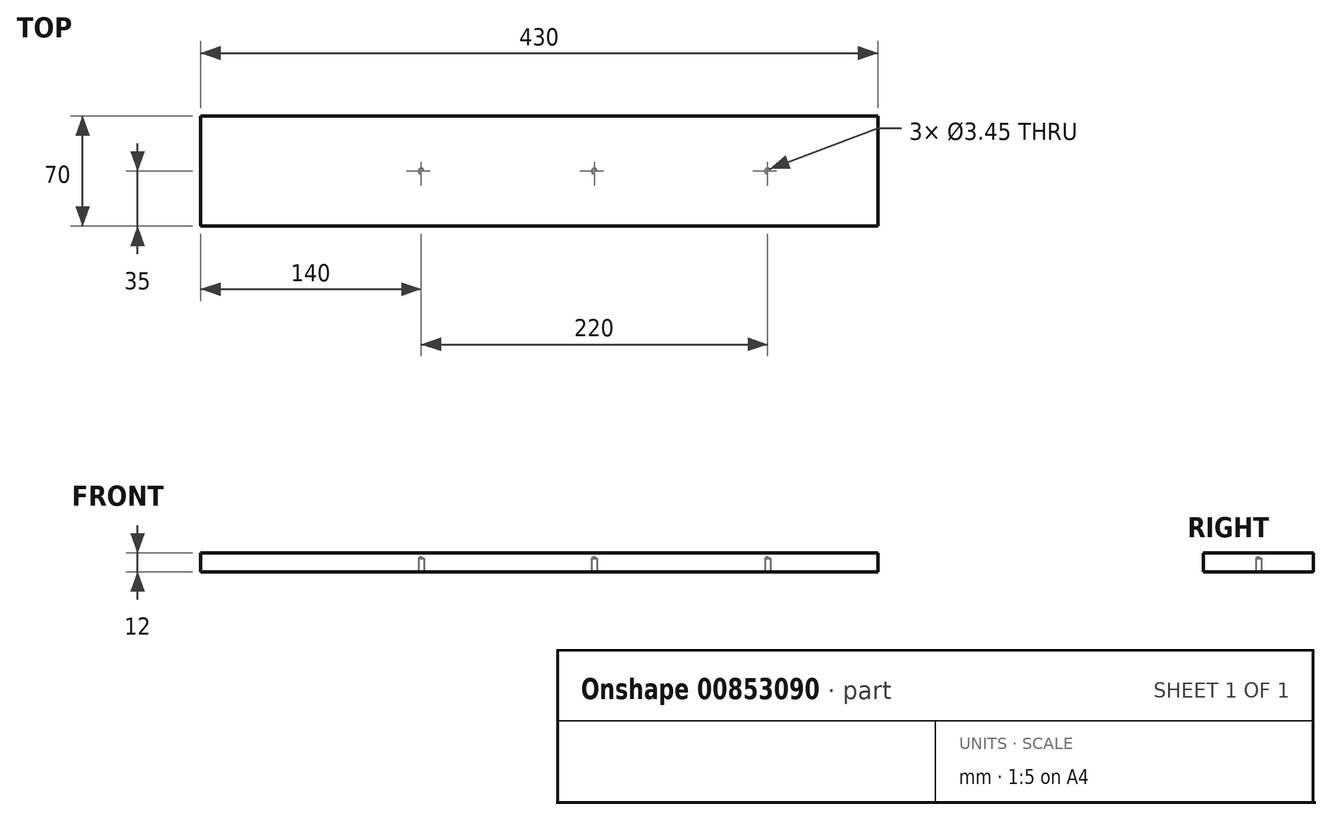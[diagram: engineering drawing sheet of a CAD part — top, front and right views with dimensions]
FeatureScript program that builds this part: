
annotation { "Feature Type Name" : "Feature", "Feature Type Description" : "" }
export const myFeature = defineFeature(function(context is Context, id is Id, definition is map)
    precondition{}
    {
        {
            var Q0;
            Q0=qCreatedBy(makeId("Top.planeOp"),FACE);
            var sketch = newSketch(context, id + "F0", { "sketchPlane" : qUnion([Q0])});
            skLineSegment(sketch, "E0.bottom", {"start": v(215, -35) * mm, "end": v(-215, -35) * mm});
            skLineSegment(sketch, "E0.top", {"start": v(215, 35) * mm, "end": v(-215, 35) * mm});
            skLineSegment(sketch, "E0.left", {"start": v(215, -35) * mm, "end": v(215, 35) * mm});
            skLineSegment(sketch, "E0.right", {"start": v(-215, -35) * mm, "end": v(-215, 35) * mm});
            skSolve(sketch);
        }
        {
            var Q0;
            Q0=makeQuery(id+"F0.imprint","IMPRINT",FACE,{"disambiguationData":[TD([[makeQuery(id+"F0.imprint","IMPRINT",EDGE,{"derivedFrom":sQuery(id+"F0.wireOp",EDGE,"E0.bottom")}),-1.0]])]});
            extrude(context, id + "F1", {"entities" : qUnion([Q0]), "depth" : 6 * mm, "offsetDistance" : 25 * mm, "hasSecondDirection" : true, "secondDirectionOppositeDirection" : true, "secondDirectionDepth" : 6 * mm});
        }
        {
            var Q0;
            Q0=makeQuery(id+"F1.opExtrude","CAP_FACE",FACE,{"disambiguationData":[OSD([sQuery(id+"F0.wireOp",EDGE,"E0.bottom"),sQuery(id+"F0.wireOp",EDGE,"E0.top"),sQuery(id+"F0.wireOp",EDGE,"E0.left"),sQuery(id+"F0.wireOp",EDGE,"E0.right")])],"isStart":true});
            var sketch = newSketch(context, id + "F2", { "sketchPlane" : qUnion([Q0])});
            skPoint(sketch, "E1", {"position": v(-75, 0) * mm});
            skPoint(sketch, "E2", {"position": v(35, 0) * mm});
            skPoint(sketch, "E3", {"position": v(145, 0) * mm});
            skSolve(sketch);
        }
        {
            var Q0;
            Q0=sQuery(id+"F2.wireOp",VERTEX,"E1");
            var Q1;
            Q1=sQuery(id+"F2.wireOp",VERTEX,"E3");
            var Q2;
            Q2=sQuery(id+"F2.wireOp",VERTEX,"E2");
            var Q3;
            Q3=makeQuery(id+"F1.opExtrude","SWEPT_BODY",BODY,{"disambiguationData":[OSD([sQuery(id+"F0.wireOp",EDGE,"E0.bottom"),sQuery(id+"F0.wireOp",EDGE,"E0.top"),sQuery(id+"F0.wireOp",EDGE,"E0.left"),sQuery(id+"F0.wireOp",EDGE,"E0.right")])]});
            hole(context, id + "F3", {"style" : HoleStyle.SIMPLE, "endStyle" : HoleEndStyle.BLIND, "standardTappedOrClearance" : lookupTablePath({ "standard" : "ANSI", "engagement" : "75%", "pitch" : "36 tpi", "size" : "#8", "type" : "Tapped" }), "standardBlindInLast" : lookupTablePath({ "standard" : "ANSI", "engagement" : "75%", "pitch" : "36 tpi", "size" : "#8", "type" : "Tapped" }), "holeDiameter" : 3.45 * mm, "majorDiameter" : 4.17 * mm, "showTappedDepth" : true, "holeDepth" : 8.53 * mm, "isTappedThrough" : true, "tappedDepth" : 6.4 * mm, "tapClearance" : 3, "startFromSketch" : true, "locations" : qUnion([Q0, Q1, Q2]), "scope" : qUnion([Q3])});
        }
    });
